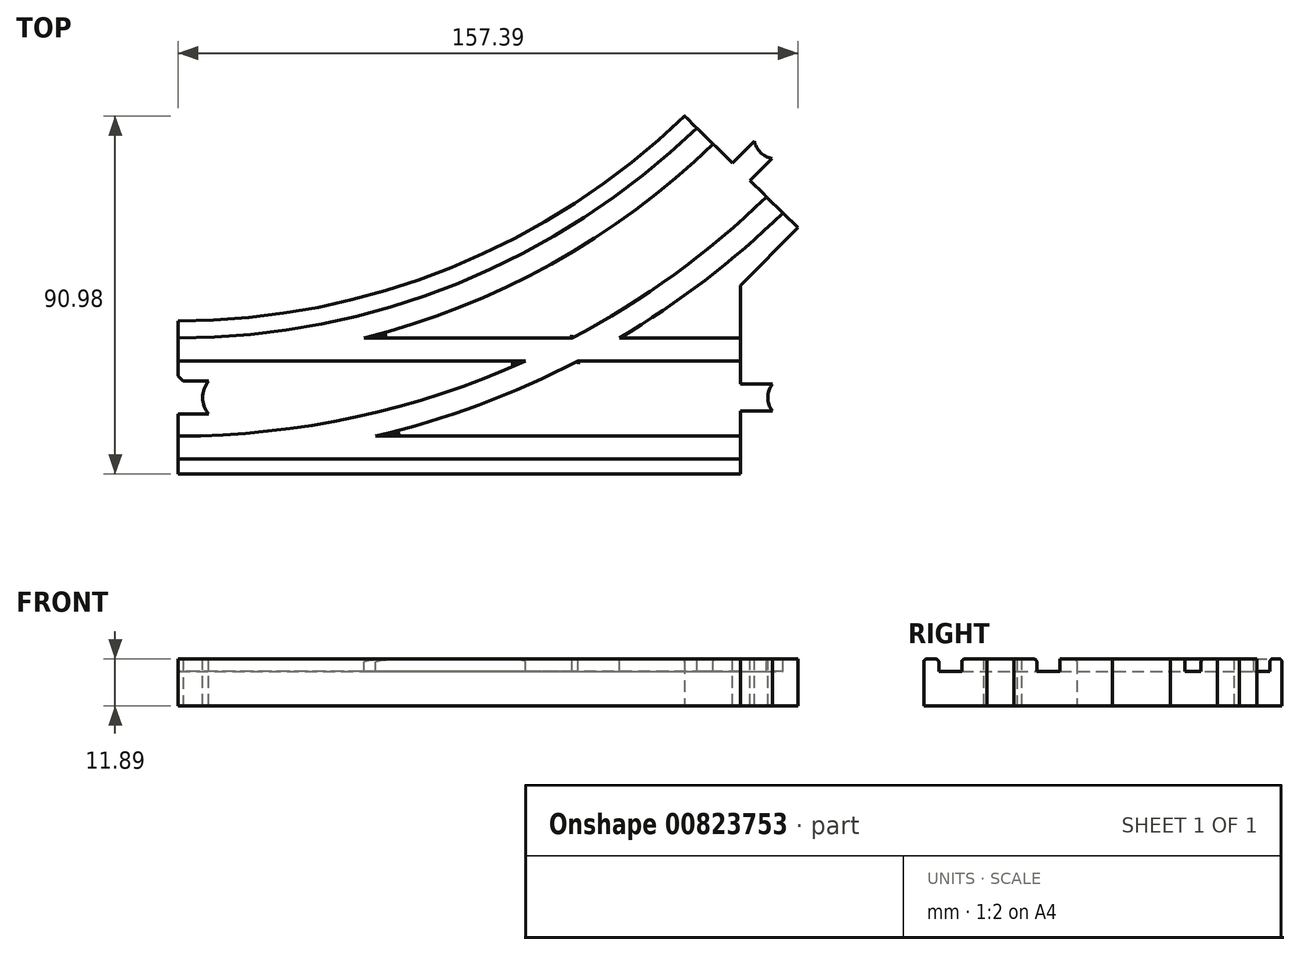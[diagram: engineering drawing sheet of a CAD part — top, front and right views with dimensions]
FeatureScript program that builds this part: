
annotation { "Feature Type Name" : "Feature", "Feature Type Description" : "" }
export const myFeature = defineFeature(function(context is Context, id is Id, definition is map)
    precondition{}
    {
        {
            var Q0;
            Q0=qCreatedBy(makeId("Top.planeOp"),FACE);
            var sketch = newSketch(context, id + "F0", { "sketchPlane" : qUnion([Q0])});
            skLineSegment(sketch, "E0", {"start": v(-98.52, 79.64) * mm, "end": v(-241.4, 79.64) * mm});
            skLineSegment(sketch, "E1", {"start": v(-241.4, 79.64) * mm, "end": v(-241.4, 118.53) * mm});
            skLineSegment(sketch, "E2", {"start": v(-98.52, 79.64) * mm, "end": v(-98.52, 127.54) * mm});
            skLineSegment(sketch, "E3", {"start": v(-98.52, 127.54) * mm, "end": v(-84, 142.24) * mm});
            skLineSegment(sketch, "E4", {"start": v(-84, 142.24) * mm, "end": v(-112.76, 170.62) * mm});
            skArc(sketch, "E5", {"start": v(-241.4, 118.53) * mm, "mid": v(-172.02, 132.1) * mm, "end": v(-112.76, 170.62) * mm});
            skSolve(sketch);
        }
        {
            var Q0;
            Q0=makeQuery(id+"F0.imprint","IMPRINT",FACE,{"disambiguationData":[TD([[makeQuery(id+"F0.imprint","IMPRINT",EDGE,{"derivedFrom":sQuery(id+"F0.wireOp",EDGE,"E0")}),-1.0]])]});
            extrude(context, id + "F1", {"entities" : qUnion([Q0]), "depth" : 11.9 * mm, "offsetDistance" : 25.4 * mm});
        }
        {
            var Q0;
            {var subQ0=sQuery(id+"F0.wireOp",EDGE,"E2");Q0=makeQuery(id+"F7.boolean.opBoolean","SPLIT",FACE,{"disambiguationData":[TD([makeQuery(id+"F5.boolean.opBoolean","COPY",FACE,{"derivedFrom":makeQuery(id+"F5.opExtrude","SWEPT_FACE",FACE,{"disambiguationData":[OSD([sQuery(id+"F3.wireOp",EDGE,"E17.0")])]})})])],"derivedFrom":makeQuery(id+"F4.boolean.opBoolean","MERGE",FACE,{"derivedFrom":[makeQuery(id+"F1.opExtrude","CAP_FACE",FACE,{"disambiguationData":[OSD([sQuery(id+"F0.wireOp",EDGE,"E0"),sQuery(id+"F0.wireOp",EDGE,"E1"),subQ0,sQuery(id+"F0.wireOp",EDGE,"E3"),sQuery(id+"F0.wireOp",EDGE,"E4"),sQuery(id+"F0.wireOp",EDGE,"E5")])],"isStart":false}),makeQuery(id+"F4.opExtrude","CAP_FACE",FACE,{"disambiguationData":[OSD([sQuery(id+"F3.wireOp",EDGE,"E7.bottom"),sQuery(id+"F3.wireOp",EDGE,"E7.top"),sQuery(id+"F3.wireOp",EDGE,"E7.left"),sQuery(id+"F3.wireOp",EDGE,"E8")])],"isStart":true})]})});}
            var Q1;
            {var subQ0=sQuery(id+"F0.wireOp",EDGE,"E5");var subQ1=sQuery(id+"F0.wireOp",EDGE,"E4");var subQ2=sQuery(id+"F0.wireOp",EDGE,"E3");var subQ3=sQuery(id+"F0.wireOp",EDGE,"E2");var subQ4=sQuery(id+"F0.wireOp",EDGE,"E1");var subQ5=sQuery(id+"F0.wireOp",EDGE,"E0");Q1=makeQuery(id+"F4.boolean.opBoolean","MERGE",FACE,{"derivedFrom":[makeQuery(id+"F1.opExtrude","CAP_FACE",FACE,{"disambiguationData":[OSD([subQ5,subQ4,subQ3,subQ2,subQ1,subQ0])],"isStart":true}),makeQuery(id+"F4.opExtrude","CAP_FACE",FACE,{"disambiguationData":[OSD([subQ5,subQ4,subQ3,subQ2,subQ1,subQ0])],"isStart":false})]});}
            cPlane(context, id + "F2", {"entities" : qUnion([Q0, Q1]), "cplaneType" : CPlaneType.MID_PLANE, "offset" : 25.4 * mm, "width" : 152.4 * mm, "height" : 152.4 * mm});
        }
        {
            var Q0;
            Q0=makeQuery(id+"F1.opExtrude","CAP_FACE",FACE,{"disambiguationData":[OSD([sQuery(id+"F0.wireOp",EDGE,"E0"),sQuery(id+"F0.wireOp",EDGE,"E1"),sQuery(id+"F0.wireOp",EDGE,"E2"),sQuery(id+"F0.wireOp",EDGE,"E3"),sQuery(id+"F0.wireOp",EDGE,"E4"),sQuery(id+"F0.wireOp",EDGE,"E5")])],"isStart":false});
            var sketch = newSketch(context, id + "F3", { "sketchPlane" : qUnion([Q0])});
            skLineSegment(sketch, "E6", {"start": v(-241.4, 99.09) * mm, "end": v(-98.52, 99.09) * mm, "construction": true});
            skLineSegment(sketch, "E7.bottom", {"start": v(-241.4, 102.51) * mm, "end": v(-249.5, 102.51) * mm});
            skLineSegment(sketch, "E7.top", {"start": v(-241.4, 95.66) * mm, "end": v(-249.5, 95.66) * mm});
            skLineSegment(sketch, "E7.left", {"start": v(-241.4, 102.51) * mm, "end": v(-241.4, 95.66) * mm});
            skLineSegment(sketch, "E7.right", {"start": v(-249.5, 102.51) * mm, "end": v(-249.5, 95.66) * mm, "construction": true});
            skCircle(sketch, "E8", {"center": v(-253.81, 99.09) * mm, "radius": 5.51 * mm});
            skLineSegment(sketch, "E9", {"start": v(-169.95, 79.64) * mm, "end": v(-169.95, 105.95) * mm, "construction": true});
            skCircle(sketch, "E10.MirrorC", {"center": v(-86.1, 99.09) * mm, "radius": 5.51 * mm});
            skLineSegment(sketch, "E11.MirrorCS", {"start": v(-98.52, 102.51) * mm, "end": v(-98.52, 95.66) * mm, "construction": true});
            skLineSegment(sketch, "E12.MirrorCS", {"start": v(-98.52, 102.51) * mm, "end": v(-90.41, 102.51) * mm});
            skLineSegment(sketch, "E13.MirrorCS", {"start": v(-98.52, 95.66) * mm, "end": v(-90.41, 95.66) * mm});
            skLineSegment(sketch, "E14.MirrorCS", {"start": v(-98.52, 95.66) * mm, "end": v(-106.62, 95.66) * mm, "construction": true});
            skLineSegment(sketch, "E15.MirrorCS", {"start": v(-98.52, 102.51) * mm, "end": v(-106.62, 102.51) * mm, "construction": true});
            skCircle(sketch, "E16.MirrorC", {"center": v(-110.94, 99.09) * mm, "radius": 5.51 * mm, "construction": true});
            skCircle(sketch, "E17.0", {"center": v(-110.94, 99.09) * mm, "radius": 6.27 * mm});
            skLineSegment(sketch, "E18.0", {"start": v(-98.52, 103.28) * mm, "end": v(-106.27, 103.28) * mm});
            skLineSegment(sketch, "E19.0", {"start": v(-98.52, 94.9) * mm, "end": v(-106.27, 94.9) * mm});
            skLineSegment(sketch, "E20", {"start": v(-98.52, 103.28) * mm, "end": v(-98.52, 94.9) * mm, "construction": true});
            skLineSegment(sketch, "E21", {"start": v(-98.38, 156.43) * mm, "end": v(-102.98, 151.77) * mm, "construction": true});
            skCircle(sketch, "E22.0", {"center": v(-107.1, 147.6) * mm, "radius": 6.27 * mm});
            skLineSegment(sketch, "E23.0", {"start": v(-101.36, 159.38) * mm, "end": v(-106.8, 153.86) * mm});
            skLineSegment(sketch, "E24.0", {"start": v(-95.4, 153.49) * mm, "end": v(-100.84, 147.97) * mm});
            skLineSegment(sketch, "E25", {"start": v(-101.36, 159.38) * mm, "end": v(-95.4, 153.49) * mm});
            skLineSegment(sketch, "E26.MirrorCS", {"start": v(-241.4, 102.51) * mm, "end": v(-233.29, 102.51) * mm, "construction": true});
            skCircle(sketch, "E27.MirrorC", {"center": v(-228.97, 99.09) * mm, "radius": 5.51 * mm, "construction": true});
            skLineSegment(sketch, "E28.MirrorCS", {"start": v(-241.4, 95.66) * mm, "end": v(-233.29, 95.66) * mm, "construction": true});
            skCircle(sketch, "E29.0", {"center": v(-228.97, 99.09) * mm, "radius": 6.27 * mm});
            skLineSegment(sketch, "E30.0", {"start": v(-241.4, 103.28) * mm, "end": v(-233.64, 103.28) * mm});
            skLineSegment(sketch, "E31.0", {"start": v(-241.4, 94.9) * mm, "end": v(-233.64, 94.9) * mm});
            skCircle(sketch, "E32.MirrorC", {"center": v(-177.24, 265.35) * mm, "radius": 5.51 * mm});
            skLineSegment(sketch, "E33.MirrorCS", {"start": v(-189.66, 268.78) * mm, "end": v(-181.55, 268.78) * mm});
            skLineSegment(sketch, "E34.MirrorCS", {"start": v(-189.66, 261.92) * mm, "end": v(-181.55, 261.92) * mm});
            skCircle(sketch, "E35.MirrorC", {"center": v(-89.63, 165.3) * mm, "radius": 5.51 * mm});
            skLineSegment(sketch, "E36.MirrorCS", {"start": v(-100.71, 158.5) * mm, "end": v(-95.06, 164.3) * mm});
            skLineSegment(sketch, "E37.MirrorCS", {"start": v(-96.29, 154.13) * mm, "end": v(-90.56, 159.86) * mm});
            skSolve(sketch);
        }
        {
            var Q0;
            {var subQ3=sQuery(id+"F3.wireOp",EDGE,"E7.left");Q0=makeQuery(id+"F3.imprint","IMPRINT",FACE,{"disambiguationData":[TD([[makeQuery(id+"F3.imprint","IMPRINT",EDGE,{"derivedFrom":subQ3}),-1.0]])]});}
            var Q1;
            {var subQ0=sQuery(id+"F3.wireOp",EDGE,"E29.0");var subQ1=makeQuery(id+"F3.imprint","INTERSECT",VERTEX,{"derivedFrom":[subQ0,sQuery(id+"F3.wireOp",EDGE,"E30.0")]});Q1=makeQuery(id+"F3.imprint","IMPRINT",FACE,{"disambiguationData":[TD([[makeQuery(id+"F3.imprint","IMPRINT",EDGE,{"disambiguationData":[TD([[subQ1,-1.0]])],"derivedFrom":subQ0}),-1.0]])]});}
            var Q2;
            Q2=makeQuery(id+"F1.opExtrude","CAP_FACE",FACE,{"disambiguationData":[OSD([sQuery(id+"F0.wireOp",EDGE,"E0"),sQuery(id+"F0.wireOp",EDGE,"E1"),sQuery(id+"F0.wireOp",EDGE,"E2"),sQuery(id+"F0.wireOp",EDGE,"E3"),sQuery(id+"F0.wireOp",EDGE,"E4"),sQuery(id+"F0.wireOp",EDGE,"E5")])],"isStart":true});
            extrude(context, id + "F4", {"entities" : qUnion([Q0, Q1]), "operationType" : NewBodyOperationType.REMOVE, "endBound" : BoundingType.THROUGH_ALL, "oppositeDirection" : true, "depth" : 25.4 * mm, "endBoundEntityFace" : qUnion([Q2]), "offsetDistance" : 25.4 * mm});
        }
        {
            var Q0;
            {var subQ0=sQuery(id+"F3.wireOp",EDGE,"E37.MirrorCS");var subQ1=sQuery(id+"F3.wireOp",EDGE,"E25");var subQ2=makeQuery(id+"F3.imprint","INTERSECT",VERTEX,{"derivedFrom":[subQ1,subQ0]});Q0=makeQuery(id+"F3.imprint","IMPRINT",FACE,{"disambiguationData":[TD([[makeQuery(id+"F3.imprint","IMPRINT",EDGE,{"disambiguationData":[TD([[subQ2,-1.0]])],"derivedFrom":subQ1}),-1.0]])]});}
            var Q1;
            {var subQ0=sQuery(id+"F3.wireOp",EDGE,"E35.MirrorC");var subQ1=makeQuery(id+"F3.imprint","INTERSECT",VERTEX,{"derivedFrom":[subQ0,sQuery(id+"F3.wireOp",EDGE,"E36.MirrorCS")]});Q1=makeQuery(id+"F3.imprint","IMPRINT",FACE,{"disambiguationData":[TD([[makeQuery(id+"F3.imprint","IMPRINT",EDGE,{"disambiguationData":[TD([[subQ1,-1.0]])],"derivedFrom":subQ0}),-1.0]])]});}
            var Q2;
            {var subQ0=sQuery(id+"F3.wireOp",EDGE,"E10.MirrorC");var subQ1=makeQuery(id+"F3.imprint","INTERSECT",VERTEX,{"derivedFrom":[subQ0,sQuery(id+"F3.wireOp",EDGE,"E12.MirrorCS")]});Q2=makeQuery(id+"F3.imprint","IMPRINT",FACE,{"disambiguationData":[TD([[makeQuery(id+"F3.imprint","IMPRINT",EDGE,{"disambiguationData":[TD([[subQ1,-1.0]])],"derivedFrom":subQ0}),-1.0]])]});}
            var Q3;
            {var subQ0=sQuery(id+"F3.wireOp",EDGE,"E12.MirrorCS");Q3=makeQuery(id+"F3.imprint","IMPRINT",FACE,{"disambiguationData":[TD([[makeQuery(id+"F3.imprint","IMPRINT",EDGE,{"derivedFrom":subQ0}),-1.0]])]});}
            var Q4;
            Q4=makeQuery(id+"F1.opExtrude","CAP_FACE",FACE,{"disambiguationData":[OSD([sQuery(id+"F0.wireOp",EDGE,"E0"),sQuery(id+"F0.wireOp",EDGE,"E1"),sQuery(id+"F0.wireOp",EDGE,"E2"),sQuery(id+"F0.wireOp",EDGE,"E3"),sQuery(id+"F0.wireOp",EDGE,"E4"),sQuery(id+"F0.wireOp",EDGE,"E5")])],"isStart":true});
            extrude(context, id + "F5", {"entities" : qUnion([Q0, Q1, Q2, Q3]), "operationType" : NewBodyOperationType.ADD, "endBound" : BoundingType.UP_TO_SURFACE, "oppositeDirection" : true, "depth" : 25.4 * mm, "endBoundEntityFace" : qUnion([Q4]), "offsetDistance" : 25.4 * mm});
        }
        {
            var Q0;
            Q0=makeQuery(id+"F4.boolean.opBoolean","MERGE",FACE,{"derivedFrom":[makeQuery(id+"F1.opExtrude","CAP_FACE",FACE,{"disambiguationData":[OSD([sQuery(id+"F0.wireOp",EDGE,"E0"),sQuery(id+"F0.wireOp",EDGE,"E1"),sQuery(id+"F0.wireOp",EDGE,"E2"),sQuery(id+"F0.wireOp",EDGE,"E3"),sQuery(id+"F0.wireOp",EDGE,"E4"),sQuery(id+"F0.wireOp",EDGE,"E5")])],"isStart":false}),makeQuery(id+"F4.opExtrude","CAP_FACE",FACE,{"disambiguationData":[OSD([sQuery(id+"F3.wireOp",EDGE,"E7.bottom"),sQuery(id+"F3.wireOp",EDGE,"E7.top"),sQuery(id+"F3.wireOp",EDGE,"E7.left"),sQuery(id+"F3.wireOp",EDGE,"E8")])],"isStart":true})]});
            var sketch = newSketch(context, id + "F6", { "sketchPlane" : qUnion([Q0])});
            skLineSegment(sketch, "E38.bottom", {"start": v(-98.52, 83.45) * mm, "end": v(-241.4, 83.45) * mm});
            skLineSegment(sketch, "E38.top", {"start": v(-98.52, 89.3) * mm, "end": v(-191.27, 89.3) * mm});
            skLineSegment(sketch, "E38.left", {"start": v(-98.52, 83.45) * mm, "end": v(-98.52, 89.3) * mm});
            skLineSegment(sketch, "E38.right", {"start": v(-241.4, 83.45) * mm, "end": v(-241.4, 89.3) * mm});
            skLineSegment(sketch, "E39.bottom", {"start": v(-98.52, 108.36) * mm, "end": v(-139.87, 108.36) * mm});
            skLineSegment(sketch, "E39.top", {"start": v(-98.52, 114.2) * mm, "end": v(-129.35, 114.2) * mm});
            skLineSegment(sketch, "E39.left", {"start": v(-98.52, 108.36) * mm, "end": v(-98.52, 114.2) * mm});
            skLineSegment(sketch, "E39.right", {"start": v(-241.4, 108.36) * mm, "end": v(-241.4, 114.2) * mm});
            skArc(sketch, "E40.0", {"start": v(-241.4, 114.2) * mm, "mid": v(-170.35, 128.11) * mm, "end": v(-109.68, 167.58) * mm});
            skArc(sketch, "E41.0", {"start": v(-194.24, 114.2) * mm, "mid": v(-146.63, 132.99) * mm, "end": v(-105.52, 163.48) * mm});
            skArc(sketch, "E42.0", {"start": v(-241.4, 89.3) * mm, "mid": v(-196.3, 94.15) * mm, "end": v(-153.24, 108.36) * mm});
            skArc(sketch, "E43.0", {"start": v(-191.27, 89.3) * mm, "mid": v(-164.98, 97.22) * mm, "end": v(-139.87, 108.36) * mm});
            skArc(sketch, "E44.trimOffspring", {"start": v(-141.3, 114.2) * mm, "mid": v(-115.35, 130.38) * mm, "end": v(-91.95, 150.08) * mm});
            skArc(sketch, "E45.trimOffspring", {"start": v(-129.35, 114.2) * mm, "mid": v(-107.62, 128.85) * mm, "end": v(-87.8, 145.98) * mm});
            skLineSegment(sketch, "E46.trimOffspring", {"start": v(-153.24, 108.36) * mm, "end": v(-241.4, 108.36) * mm});
            skLineSegment(sketch, "E47.trimOffspring", {"start": v(-141.3, 114.2) * mm, "end": v(-194.24, 114.2) * mm});
            skSolve(sketch);
        }
        {
            var Q0;
            Q0=makeQuery(id+"F6.imprint","IMPRINT",FACE,{"disambiguationData":[TD([[makeQuery(id+"F6.imprint","IMPRINT",EDGE,{"derivedFrom":sQuery(id+"F6.wireOp",EDGE,"E38.bottom")}),-1.0]])]});
            extrude(context, id + "F7", {"entities" : qUnion([Q0]), "operationType" : NewBodyOperationType.REMOVE, "oppositeDirection" : true, "depth" : 3.17 * mm, "offsetDistance" : 25.4 * mm});
        }
        {
            var Q0;
            Q0=makeQuery(id+"F4.boolean.opBoolean","COPY",EDGE,{"derivedFrom":makeQuery(id+"F4.opExtrude","SWEPT_EDGE",EDGE,{"disambiguationData":[OSD([sQuery(id+"F0.wireOp",EDGE,"E1"),sQuery(id+"F3.wireOp",EDGE,"E30.0")])]})});
            var Q1;
            Q1=makeQuery(id+"F4.boolean.opBoolean","COPY",EDGE,{"derivedFrom":makeQuery(id+"F4.opExtrude","SWEPT_EDGE",EDGE,{"disambiguationData":[OSD([sQuery(id+"F0.wireOp",EDGE,"E1"),sQuery(id+"F3.wireOp",EDGE,"E31.0")])]})});
            chamfer(context, id + "F8", {"entities" : qUnion([Q0, Q1]), "width" : 1.27 * mm, "tangentPropagation" : true});
        }
        {
            var Q0;
            Q0=makeQuery(id+"F1.opExtrude","CAP_EDGE",EDGE,{"disambiguationData":[OSD([sQuery(id+"F0.wireOp",EDGE,"E5")])],"isStart":false});
            var Q1;
            Q1=makeQuery(id+"F7.boolean.opBoolean","COPY",EDGE,{"derivedFrom":makeQuery(id+"F7.opExtrude","CAP_EDGE",EDGE,{"disambiguationData":[OSD([sQuery(id+"F6.wireOp",EDGE,"E40.0")])],"isStart":true})});
            var Q2;
            Q2=makeQuery(id+"F7.boolean.opBoolean","COPY",EDGE,{"derivedFrom":makeQuery(id+"F7.opExtrude","CAP_EDGE",EDGE,{"disambiguationData":[OSD([sQuery(id+"F6.wireOp",EDGE,"E41.0")])],"isStart":true})});
            var Q3;
            Q3=makeQuery(id+"F7.boolean.opBoolean","COPY",EDGE,{"derivedFrom":makeQuery(id+"F7.opExtrude","CAP_EDGE",EDGE,{"disambiguationData":[OSD([sQuery(id+"F6.wireOp",EDGE,"E44.trimOffspring")])],"isStart":true})});
            var Q4;
            Q4=makeQuery(id+"F7.boolean.opBoolean","COPY",EDGE,{"derivedFrom":makeQuery(id+"F7.opExtrude","CAP_EDGE",EDGE,{"disambiguationData":[OSD([sQuery(id+"F6.wireOp",EDGE,"E45.trimOffspring")])],"isStart":true})});
            var Q5;
            Q5=makeQuery(id+"F7.boolean.opBoolean","COPY",EDGE,{"derivedFrom":makeQuery(id+"F7.opExtrude","CAP_EDGE",EDGE,{"disambiguationData":[OSD([sQuery(id+"F6.wireOp",EDGE,"E39.top")])],"isStart":true})});
            var Q6;
            Q6=makeQuery(id+"F7.boolean.opBoolean","COPY",EDGE,{"derivedFrom":makeQuery(id+"F7.opExtrude","CAP_EDGE",EDGE,{"disambiguationData":[OSD([sQuery(id+"F6.wireOp",EDGE,"E39.bottom")])],"isStart":true})});
            var Q7;
            Q7=makeQuery(id+"F7.boolean.opBoolean","COPY",EDGE,{"derivedFrom":makeQuery(id+"F7.opExtrude","CAP_EDGE",EDGE,{"disambiguationData":[OSD([sQuery(id+"F6.wireOp",EDGE,"E43.0")])],"isStart":true})});
            var Q8;
            Q8=makeQuery(id+"F7.boolean.opBoolean","COPY",EDGE,{"derivedFrom":makeQuery(id+"F7.opExtrude","CAP_EDGE",EDGE,{"disambiguationData":[OSD([sQuery(id+"F6.wireOp",EDGE,"E47.trimOffspring")])],"isStart":true})});
            var Q9;
            Q9=makeQuery(id+"F7.boolean.opBoolean","COPY",EDGE,{"derivedFrom":makeQuery(id+"F7.opExtrude","CAP_EDGE",EDGE,{"disambiguationData":[OSD([sQuery(id+"F6.wireOp",EDGE,"E46.trimOffspring")])],"isStart":true})});
            var Q10;
            Q10=makeQuery(id+"F7.boolean.opBoolean","COPY",EDGE,{"derivedFrom":makeQuery(id+"F7.opExtrude","CAP_EDGE",EDGE,{"disambiguationData":[OSD([sQuery(id+"F6.wireOp",EDGE,"E42.0")])],"isStart":true})});
            var Q11;
            Q11=makeQuery(id+"F7.boolean.opBoolean","COPY",EDGE,{"derivedFrom":makeQuery(id+"F7.opExtrude","CAP_EDGE",EDGE,{"disambiguationData":[OSD([sQuery(id+"F6.wireOp",EDGE,"E38.top")])],"isStart":true})});
            var Q12;
            Q12=makeQuery(id+"F7.boolean.opBoolean","COPY",EDGE,{"derivedFrom":makeQuery(id+"F7.opExtrude","CAP_EDGE",EDGE,{"disambiguationData":[OSD([sQuery(id+"F6.wireOp",EDGE,"E38.bottom")])],"isStart":true})});
            var Q13;
            Q13=makeQuery(id+"F1.opExtrude","CAP_EDGE",EDGE,{"disambiguationData":[OSD([sQuery(id+"F0.wireOp",EDGE,"E0")])],"isStart":false});
            fillet(context, id + "F9", {"entities" : qUnion([Q0, Q1, Q2, Q3, Q4, Q5, Q6, Q7, Q8, Q9, Q10, Q11, Q12, Q13]), "radius" : 0.76 * mm, "tangentPropagation" : true, "allowEdgeOverflow" : false});
        }
    });
